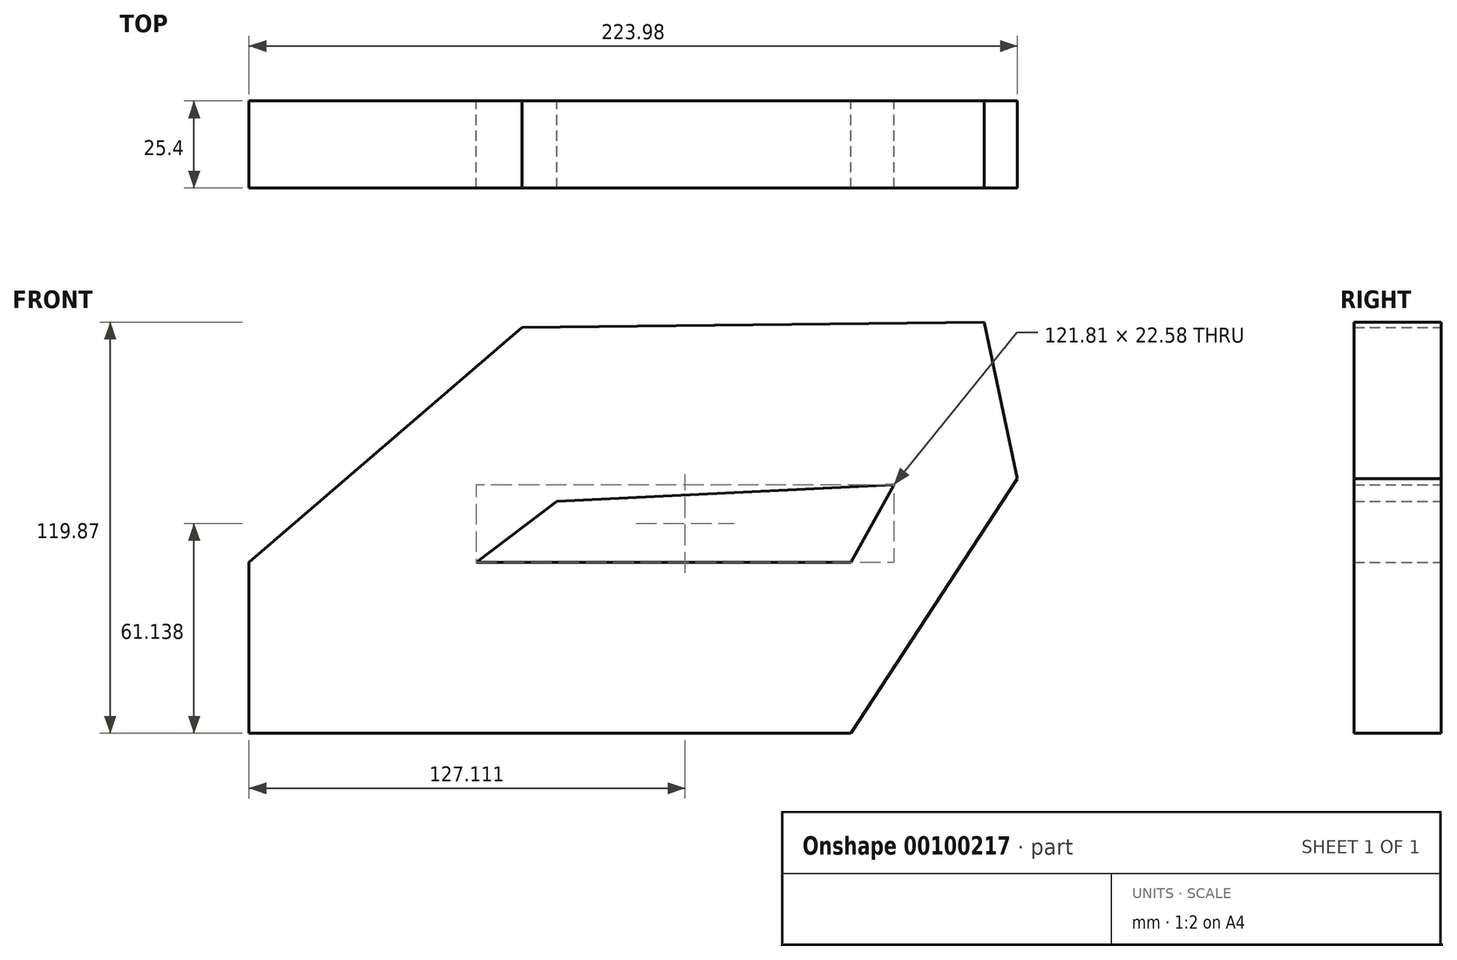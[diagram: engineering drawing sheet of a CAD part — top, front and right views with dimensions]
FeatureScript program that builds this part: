
annotation { "Feature Type Name" : "Feature", "Feature Type Description" : "" }
export const myFeature = defineFeature(function(context is Context, id is Id, definition is map)
    precondition{}
    {
        {
            var Q0;
            Q0=qCreatedBy(makeId("Front.planeOp"),FACE);
            var sketch = newSketch(context, id + "F0", { "sketchPlane" : qUnion([Q0])});
            skLineSegment(sketch, "E0.bottom", {"start": v(-53.06, 6.37) * mm, "end": v(122.45, 6.37) * mm});
            skLineSegment(sketch, "E0.top", {"start": v(-53.06, -43.48) * mm, "end": v(122.45, -43.48) * mm});
            skLineSegment(sketch, "E0.left", {"start": v(-53.06, 6.37) * mm, "end": v(-53.06, -43.48) * mm});
            skLineSegment(sketch, "E0.right", {"start": v(122.45, 6.37) * mm, "end": v(122.45, -43.48) * mm});
            skLineSegment(sketch, "E1", {"start": v(-53.06, 6.37) * mm, "end": v(26.53, 74.75) * mm});
            skLineSegment(sketch, "E2", {"start": v(-53.06, -43.48) * mm, "end": v(36.73, 24.12) * mm});
            skLineSegment(sketch, "E3", {"start": v(122.45, 6.37) * mm, "end": v(161.22, 76.39) * mm});
            skLineSegment(sketch, "E4", {"start": v(122.45, -43.48) * mm, "end": v(170.92, 30.72) * mm});
            skLineSegment(sketch, "E5", {"start": v(36.73, 24.12) * mm, "end": v(170.92, 30.72) * mm});
            skLineSegment(sketch, "E6", {"start": v(26.53, 74.75) * mm, "end": v(161.22, 76.39) * mm});
            skLineSegment(sketch, "E7", {"start": v(26.53, 74.75) * mm, "end": v(36.73, 24.12) * mm});
            skLineSegment(sketch, "E8", {"start": v(161.22, 76.39) * mm, "end": v(170.92, 30.72) * mm});
            skSolve(sketch);
        }
        {
            var Q0;
            Q0 = qSketchRegion(id + "F0", true);
            extrude(context, id + "F1", {"entities" : qUnion([Q0]), "depth" : 25.4 * mm});
        }
    });
